# Revit family: Combination_Unit-Bradley_Corp-5912
name_source: partatom
category: Specialty Equipment
revit_build: Autodesk Revit 2018 (Build: 20170223_1515(x64)
units: mm (PartAtom-declared; Revit-internal decimal feet)

## family parameters
Cut with Voids When Loaded = No
Host = Face
Part Type = Normal
Room Calculation Point = No
Round Connector Dimension = Use Diameter
Shared = No

## types (2) — shared parameters
ADA Compliant = Yes
Assembly Code = C1030200
Buy American Act = Yes
Cabinet Material = Metal - Bradley Corp - Stainless Steel Satin
Default Elevation = 48"
Depth = 4 1/2"
Depth of which projects = 1/4"
Description = Combination Unit
Flange Width = 1"
Height = 30 5/8"
Low Emitting Material = No
Manufacturer = Bradley Corporation
MasterFormat Number = 10 28 13. 13
MasterFormat Title = Commercial Toilet Accessories
OmniClass Code = 23.31.25.00
OmniClass Title = Toilet and Bath Specialties
URL = http://www.bradleycorp.com
Version = 1.0
Void Depth = 4 1/2"
Void Height = 28 7/8"
Void Width = 15 3/8"
Warranty Information = Complete unit, excepting mirrors warranted for one year.
Width = 17 1/8"
zero-valued in all types: Percentage of Recycled Content

## per-type parameters (varying)
| type | Door Side Indicator | Model |
| Right Hand Spindles | 1 | 5912-000000 |
| Left Hand Spindles | 2 | 5912-690000 |

note: column(s) folded — value = type name in every type: Type Comments

## geometry (parser evidence)
native form markers: Sweep x2
no freeform markers — native parametric forms only
